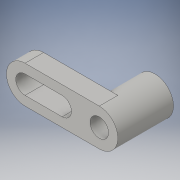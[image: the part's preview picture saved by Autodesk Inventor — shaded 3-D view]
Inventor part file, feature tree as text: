
AUTODESK INVENTOR PART (.ipt)
format: ipt  version: 2016 (Build 200138000, 138)  size: 124,928 bytes
history: native  units: in
note: dims shown in document units (in); Inventor stores cm internally (conversion verified against a paired STEP export)
features: sketch x4, extrude x3, hole x1
ambient origin geometry x8: Origin, YZ Plane, XZ Plane, XY Plane, X Axis, Y Axis, Z Axis, Center Point
bodies: Solid1 (feature_tree)
feature tree (8):
  extrude  "Extrusion1"  Depth=0.5in
  extrude  "Extrusion2"  Depth=1.0in
  extrude  "Extrusion3"  Depth=0.5in TaperAngle=0.0deg
  hole  "Hole1"  [1 undecoded]
  sketch  "Sketch1"  dims[d0=2.0in d1=0.5in]
  sketch  "Sketch2"  dims[d2=0.5in d3=0.0in d4=1.0in]
  sketch  "Sketch3"  dims[d5=0.25in d6=0.5in d7=0.0in]
  sketch  "Sketch4"  dims[d8=1.0in d9=1.0in d10=0.0in d11=0.5in d12=0.75in d13=0.375in d14=0.25in d15=0.5635in d16=1.0in d17=0.8108in]
note: 1 required parameter value undecoded (feature->parameter linkage not recoverable at this tier; creation-order binding heuristic only, values carry confidence <= 0.55)
